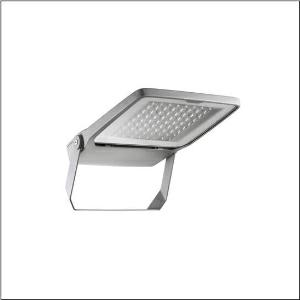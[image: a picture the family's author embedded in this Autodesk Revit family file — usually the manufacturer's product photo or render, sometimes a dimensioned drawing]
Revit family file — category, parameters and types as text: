
# Revit family: floodlight_fl_20_mini___pl43_5xa7671b2a1ac_fa9e
name_source: partatom
category: Lighting Fixtures
units: mm (PartAtom-declared; Revit-internal decimal feet)

## family parameters
Cut with Voids When Loaded = No
Host = Face
Light Source = No
Part Type = Normal
Room Calculation Point = No
Round Connector Dimension = Use Diameter
Shared = No

## types (1)
- Floodlight FL 20 mini  PL43 (1 x LED 4000K / CRI = 70 (unbekannt), 6650 lm, 4000K)
    Apparent Load = 51 VA
    CIE Flux Codes = 32 74 99 100 100
    Color Rendering = 70
    Color Temperature = 4000K
    Default Elevation = 1800 mm
    Description = Floodlight FL 20 mini, floodlight, primary light control with lens, of plastic, primary optical cover: protective disc, of toughened safety glass, transparent, light distribution: PL43, light emission: direct distribution, primary light characteristic: asymmetric, installation type: surface-mounted, LED, High Power LED, rated luminous flux: 6.650lm, luminous efficacy: 130lm/W, light colour: 740, colour temperature: 4000K, control gear: ECG Basic, control: power reduction, overheat protection, electronic power reduction, with terminal, 5-pole, max. 2.5mm², mains connection: 220..240V, AC, 50/60Hz, rated input power: 51W, LED unit, of diecast aluminium, powder-coated, Siteco® metallic grey (DB 702S), corrosivity category C5 mid according to DIN EN ISO 12944, incl. 1x M20 cable gland for cable Ø 6.5..12mm, length: 446mm, width: 355mm, height: 62mm, housing frame, of diecast aluminium, powder-coated, Siteco® metallic grey (DB 702S), mounting bracket, of steel, powder-coated, Siteco® metallic grey (DB 702S), ON/OFF, protection rating (complete): IP66, insulation class (complete): insulation class I (protective earthing), certification: CE, ENEC, VDE, protection symbol: D, permissible operating ambient temperature: -40..+40°C, permissible operating ambient temperature for outdoor applications: -40..+50°C, standard: DIN EN 12944, packaging unit: 1 piece

Light Distribution: PL43
    Height = 62 mm  [stored 0.203412 ft]
    Lamp = 1 x LED 4000K / CRI >= 70 (unbekannt)
    Lamp Light Flux = 6650 lm
    Lamp count = 1
    Length = 467 mm
    Luminous efficacy = 130 lm/W
    Manufacturer = Siteco
    ModVariant = No
    Model = 5XA7671B2A1AC
    Mounting Place = Wall
    Mounting Type = Surface mounted
    Number of Poles = 1
    OnlyDefault = Yes
    Power Factor = 1
    Product Name = Floodlight FL 20 mini | PL43
    Product group = floodlight | wall mounted
    ProductGroupID = 2001
    Protection Class = Protection class I
    Protection Degree = IP 66
    RLX_Detail_Level = 1
    RLX_Emergency_Light_Flux = 0 lm
    RLX_Emergency_Type = 0
    RLX_Emergency_Type_DB = No
    RlxData = <blob elided: 70949 chars, md5=1c5f5e33>
    Socket = socket
    Standby Power = 0 W
    System Light Flux = 6650 lm
    System Power = 51 W
    Type Comments = Product without accessories
    Type Image = l_1005948.jpg
    URL = http://relux.com
    VarID = ---
    Voltage = 0 V
    Weight = 0.00 kg
    Width = 335 mm

note: [stored X ft] marks values corroborated as IEEE doubles in the binary element streams (Revit-internal decimal feet)

## geometry (parser evidence)
native form markers: Blend x4, Sweep x12
no freeform markers — native parametric forms only
